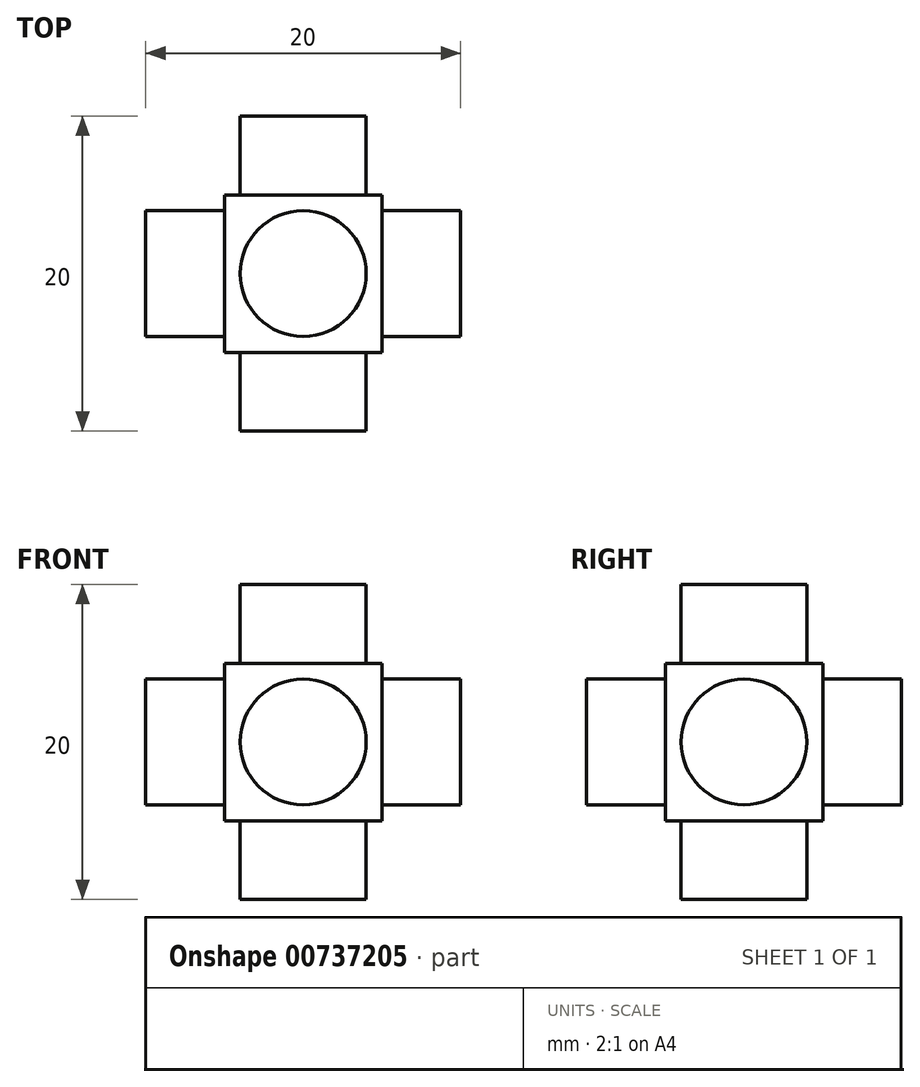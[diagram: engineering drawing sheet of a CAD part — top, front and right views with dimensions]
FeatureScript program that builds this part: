
annotation { "Feature Type Name" : "Feature", "Feature Type Description" : "" }
export const myFeature = defineFeature(function(context is Context, id is Id, definition is map)
    precondition{}
    {
        {
            var Q0;
            Q0=qCreatedBy(makeId("Top.planeOp"),FACE);
            var sketch = newSketch(context, id + "F0", { "sketchPlane" : qUnion([Q0])});
            skLineSegment(sketch, "E0.bottom", {"start": v(-5, -5) * mm, "end": v(5, -5) * mm});
            skLineSegment(sketch, "E0.top", {"start": v(-5, 5) * mm, "end": v(5, 5) * mm});
            skLineSegment(sketch, "E0.left", {"start": v(-5, -5) * mm, "end": v(-5, 5) * mm});
            skLineSegment(sketch, "E0.right", {"start": v(5, -5) * mm, "end": v(5, 5) * mm});
            skPoint(sketch, "E0.middle", {"position": v(0, 0) * mm});
            skSolve(sketch);
        }
        {
            var Q0;
            Q0 = qSketchRegion(id + "F0", true);
            extrude(context, id + "F1", {"entities" : qUnion([Q0]), "depth" : 10 * mm, "offsetDistance" : 25 * mm});
        }
        {
            var Q0;
            Q0=makeQuery(id+"F1.opExtrude","SWEPT_FACE",FACE,{"disambiguationData":[OSD([sQuery(id+"F0.wireOp",EDGE,"E0.top")])]});
            var sketch = newSketch(context, id + "F2", { "sketchPlane" : qUnion([Q0])});
            skCircle(sketch, "E1", {"center": v(0, 5) * mm, "radius": 4 * mm});
            skPoint(sketch, "E1.centerSnap0", {"position": v(-5, 5) * mm});
            skSolve(sketch);
        }
        {
            var Q0;
            Q0 = qSketchRegion(id + "F2", true);
            extrude(context, id + "F3", {"entities" : qUnion([Q0]), "operationType" : NewBodyOperationType.ADD, "depth" : 5 * mm, "offsetDistance" : 25 * mm});
        }
        {
            var Q0;
            Q0=makeQuery(id+"F1.opExtrude","CAP_FACE",FACE,{"disambiguationData":[OSD([sQuery(id+"F0.wireOp",EDGE,"E0.bottom"),sQuery(id+"F0.wireOp",EDGE,"E0.top"),sQuery(id+"F0.wireOp",EDGE,"E0.left"),sQuery(id+"F0.wireOp",EDGE,"E0.right")])],"isStart":false});
            var sketch = newSketch(context, id + "F4", { "sketchPlane" : qUnion([Q0])});
            skCircle(sketch, "E2", {"center": v(0, 0) * mm, "radius": 4 * mm});
            skSolve(sketch);
        }
        {
            var Q0;
            Q0=makeQuery(id+"F4.imprint","IMPRINT",FACE,{"disambiguationData":[TD([[makeQuery(id+"F4.imprint","IMPRINT",EDGE,{"derivedFrom":sQuery(id+"F4.wireOp",EDGE,"E2")}),1.0]])]});
            extrude(context, id + "F5", {"entities" : qUnion([Q0]), "operationType" : NewBodyOperationType.ADD, "depth" : 5 * mm, "offsetDistance" : 25 * mm});
        }
        {
            var Q0;
            Q0=makeQuery(id+"F1.opExtrude","SWEPT_FACE",FACE,{"disambiguationData":[OSD([sQuery(id+"F0.wireOp",EDGE,"E0.left")])]});
            var sketch = newSketch(context, id + "F6", { "sketchPlane" : qUnion([Q0])});
            skCircle(sketch, "E3", {"center": v(0, 5) * mm, "radius": 4 * mm});
            skPoint(sketch, "E3.centerSnap0", {"position": v(5, 5) * mm});
            skSolve(sketch);
        }
        {
            var Q0;
            Q0=makeQuery(id+"F6.imprint","IMPRINT",FACE,{"disambiguationData":[TD([[makeQuery(id+"F6.imprint","IMPRINT",EDGE,{"derivedFrom":sQuery(id+"F6.wireOp",EDGE,"E3")}),1.0]])]});
            extrude(context, id + "F7", {"entities" : qUnion([Q0]), "operationType" : NewBodyOperationType.ADD, "depth" : 5 * mm, "offsetDistance" : 25 * mm});
        }
        {
            var Q0;
            Q0=makeQuery(id+"F1.opExtrude","CAP_FACE",FACE,{"disambiguationData":[OSD([sQuery(id+"F0.wireOp",EDGE,"E0.bottom"),sQuery(id+"F0.wireOp",EDGE,"E0.top"),sQuery(id+"F0.wireOp",EDGE,"E0.left"),sQuery(id+"F0.wireOp",EDGE,"E0.right")])],"isStart":true});
            var sketch = newSketch(context, id + "F8", { "sketchPlane" : qUnion([Q0])});
            skCircle(sketch, "E4", {"center": v(0, 0) * mm, "radius": 4 * mm});
            skSolve(sketch);
        }
        {
            var Q0;
            Q0=makeQuery(id+"F8.imprint","IMPRINT",FACE,{"disambiguationData":[TD([[makeQuery(id+"F8.imprint","IMPRINT",EDGE,{"derivedFrom":sQuery(id+"F8.wireOp",EDGE,"E4")}),1.0]])]});
            extrude(context, id + "F9", {"entities" : qUnion([Q0]), "operationType" : NewBodyOperationType.ADD, "depth" : 5 * mm, "offsetDistance" : 25 * mm});
        }
        {
            var Q0;
            Q0=makeQuery(id+"F1.opExtrude","SWEPT_FACE",FACE,{"disambiguationData":[OSD([sQuery(id+"F0.wireOp",EDGE,"E0.right")])]});
            var sketch = newSketch(context, id + "F10", { "sketchPlane" : qUnion([Q0])});
            skCircle(sketch, "E5", {"center": v(0, 5) * mm, "radius": 4 * mm});
            skPoint(sketch, "E5.centerSnap0", {"position": v(-5, 5) * mm});
            skSolve(sketch);
        }
        {
            var Q0;
            Q0=makeQuery(id+"F10.imprint","IMPRINT",FACE,{"disambiguationData":[TD([[makeQuery(id+"F10.imprint","IMPRINT",EDGE,{"derivedFrom":sQuery(id+"F10.wireOp",EDGE,"E5")}),1.0]])]});
            extrude(context, id + "F11", {"entities" : qUnion([Q0]), "operationType" : NewBodyOperationType.ADD, "depth" : 5 * mm, "offsetDistance" : 25 * mm});
        }
        {
            var Q0;
            Q0=makeQuery(id+"F1.opExtrude","SWEPT_FACE",FACE,{"disambiguationData":[OSD([sQuery(id+"F0.wireOp",EDGE,"E0.bottom")])]});
            var sketch = newSketch(context, id + "F12", { "sketchPlane" : qUnion([Q0])});
            skCircle(sketch, "E6", {"center": v(0, 5) * mm, "radius": 4 * mm});
            skPoint(sketch, "E6.centerSnap0", {"position": v(-5, 5) * mm});
            skSolve(sketch);
        }
        {
            var Q0;
            Q0=makeQuery(id+"F12.imprint","IMPRINT",FACE,{"disambiguationData":[TD([[makeQuery(id+"F12.imprint","IMPRINT",EDGE,{"derivedFrom":sQuery(id+"F12.wireOp",EDGE,"E6")}),1.0]])]});
            extrude(context, id + "F13", {"entities" : qUnion([Q0]), "operationType" : NewBodyOperationType.ADD, "depth" : 5 * mm, "offsetDistance" : 25 * mm});
        }
    });
